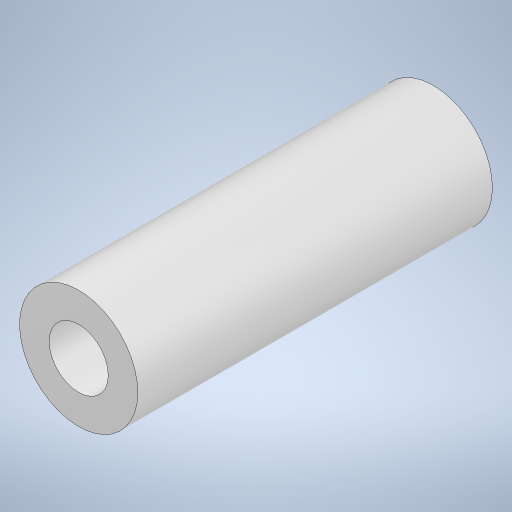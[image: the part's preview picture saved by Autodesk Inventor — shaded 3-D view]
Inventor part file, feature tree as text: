
AUTODESK INVENTOR PART (.ipt)
format: ipt  version: 2023 (Build 270158000, 158)  size: 215,040 bytes
history: native  units: mm
features: extrude x1, sketch x1
ambient origin geometry x8: Origin, YZ Plane, XZ Plane, XY Plane, X Axis, Y Axis, Z Axis, Center Point
bodies: Solid1 (feature_tree)
feature tree (2):
  extrude  "Extrusion1"  Depth=18.0mm
  sketch  "Sketch1"  dims[d0=3.0mm d1=6.0mm d2=18.0mm d3=0.0mm]
